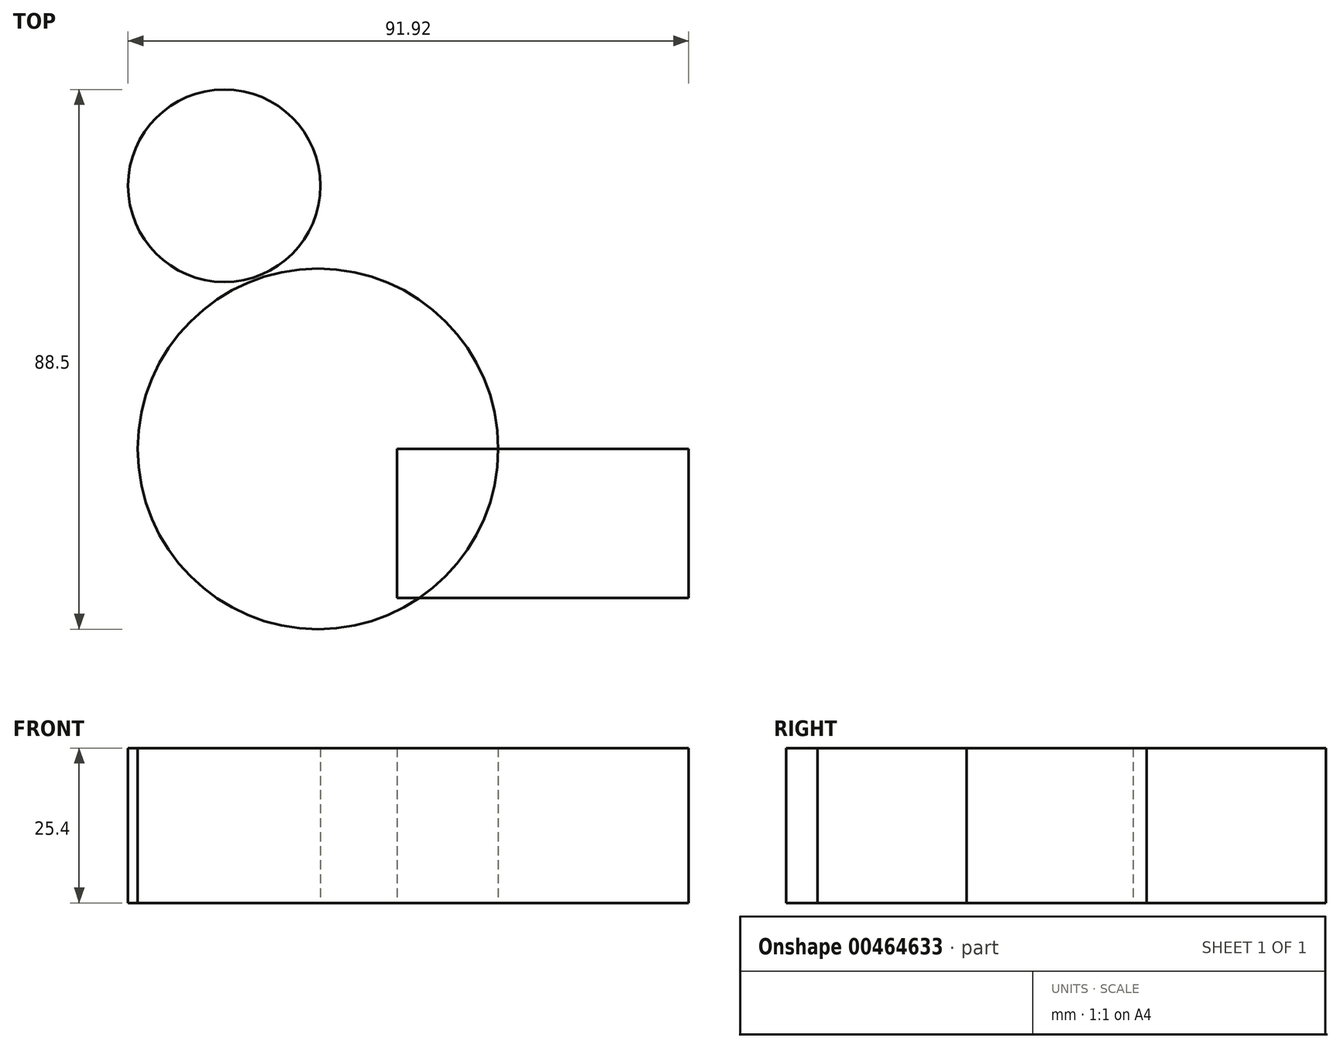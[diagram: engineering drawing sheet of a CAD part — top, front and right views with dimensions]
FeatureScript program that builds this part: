
annotation { "Feature Type Name" : "Feature", "Feature Type Description" : "" }
export const myFeature = defineFeature(function(context is Context, id is Id, definition is map)
    precondition{}
    {
        {
            var Q0;
            Q0=qCreatedBy(makeId("Top.planeOp"),FACE);
            var sketch = newSketch(context, id + "F0", { "sketchPlane" : qUnion([Q0])});
            skCircle(sketch, "E0", {"center": v(0, 0) * mm, "radius": 29.57 * mm});
            skSolve(sketch);
        }
        {
            var Q0;
            Q0=qCreatedBy(makeId("Top.planeOp"),FACE);
            var sketch = newSketch(context, id + "F1", { "sketchPlane" : qUnion([Q0])});
            skCircle(sketch, "E1", {"center": v(-15.36, 43.14) * mm, "radius": 15.78 * mm});
            skSolve(sketch);
        }
        {
            var Q0;
            Q0=qCreatedBy(makeId("Top.planeOp"),FACE);
            var sketch = newSketch(context, id + "F2", { "sketchPlane" : qUnion([Q0])});
            skCircle(sketch, "E2", {"center": v(40.2, 28.72) * mm, "radius": 30.67 * mm});
            skLineSegment(sketch, "E3.bottom", {"start": v(60.78, 0) * mm, "end": v(12.96, 0) * mm});
            skLineSegment(sketch, "E3.top", {"start": v(60.78, -24.44) * mm, "end": v(12.96, -24.44) * mm});
            skLineSegment(sketch, "E3.left", {"start": v(60.78, 0) * mm, "end": v(60.78, -24.44) * mm});
            skLineSegment(sketch, "E3.right", {"start": v(12.96, 0) * mm, "end": v(12.96, -24.44) * mm});
            skSolve(sketch);
        }
        {
            var Q0;
            Q0=makeQuery(id+"F0.imprint","IMPRINT",FACE,{"disambiguationData":[TD([[makeQuery(id+"F0.imprint","IMPRINT",EDGE,{"derivedFrom":sQuery(id+"F0.wireOp",EDGE,"E0")}),1.0]])]});
            var Q1;
            Q1=makeQuery(id+"F2.imprint","IMPRINT",FACE,{"disambiguationData":[TD([[makeQuery(id+"F2.imprint","IMPRINT",EDGE,{"derivedFrom":sQuery(id+"F2.wireOp",EDGE,"E3.top")}),-1.0]])]});
            var Q2;
            {var subQ0=sQuery(id+"F2.wireOp",EDGE,"E3.bottom");var subQ1=sQuery(id+"F2.wireOp",EDGE,"E2");var subQ2=makeQuery(id+"F2.imprint","INTERSECT",VERTEX,{"disambiguationData":[OD(0.0)],"derivedFrom":[subQ1,subQ0]});Q2=makeQuery(id+"F2.imprint","IMPRINT",FACE,{"disambiguationData":[TD([[makeQuery(id+"F2.imprint","IMPRINT",EDGE,{"disambiguationData":[TD([[subQ2,-1.0]])],"derivedFrom":subQ1}),1.0]])]});}
            var Q3;
            Q3=makeQuery(id+"F1.imprint","IMPRINT",FACE,{"disambiguationData":[TD([[makeQuery(id+"F1.imprint","IMPRINT",EDGE,{"derivedFrom":sQuery(id+"F1.wireOp",EDGE,"E1")}),1.0]])]});
            extrude(context, id + "F3", {"entities" : qUnion([Q0, Q1, Q2, Q3]), "depth" : 25.4 * mm});
        }
    });
